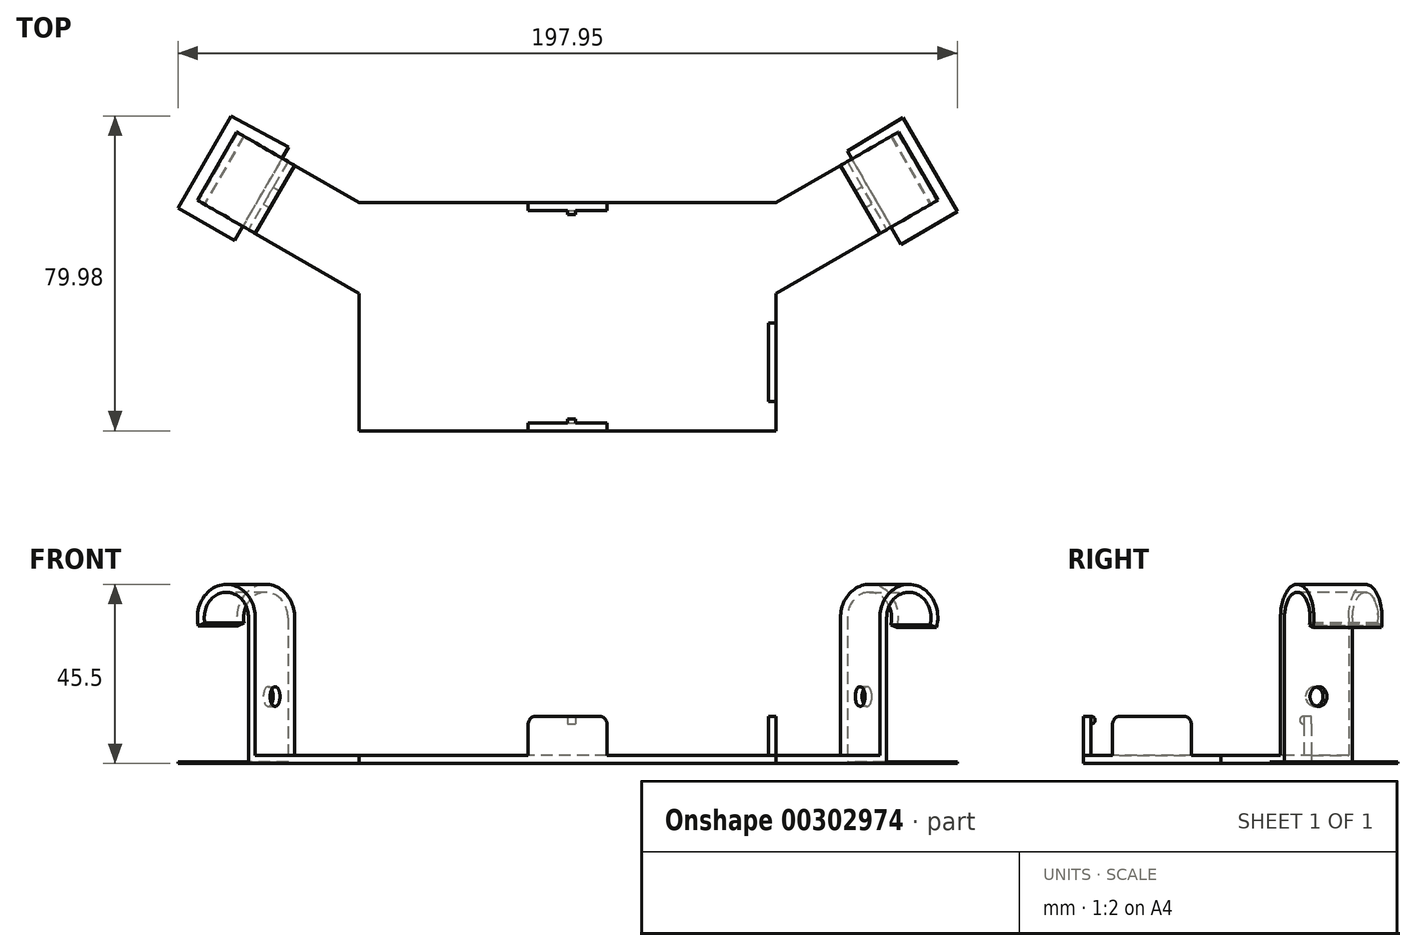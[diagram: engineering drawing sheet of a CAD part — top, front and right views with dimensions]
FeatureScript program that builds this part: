
annotation { "Feature Type Name" : "Feature", "Feature Type Description" : "" }
export const myFeature = defineFeature(function(context is Context, id is Id, definition is map)
    precondition{}
    {
        {
            var Q0;
            Q0=qCreatedBy(makeId("Top.planeOp"),FACE);
            var sketch = newSketch(context, id + "F0", { "sketchPlane" : qUnion([Q0])});
            skLineSegment(sketch, "E0.0", {"start": v(-14.9, 234.67) * mm, "end": v(190.1, -120.4) * mm, "construction": true});
            skLineSegment(sketch, "E0.1", {"start": v(190.1, -120.4) * mm, "end": v(-219.9, -120.4) * mm, "construction": true});
            skLineSegment(sketch, "E0.2", {"start": v(-219.9, -120.4) * mm, "end": v(-14.9, 234.67) * mm, "construction": true});
            skPoint(sketch, "E0.0.midPoint", {"position": v(87.6, 57.13) * mm});
            skPoint(sketch, "E1.endSnap0", {"position": v(-14.9, -120.4) * mm});
            skLineSegment(sketch, "E2", {"start": v(-14.9, 234.67) * mm, "end": v(-14.9, 59.17) * mm, "construction": true});
            skLineSegment(sketch, "E3.bottom", {"start": v(38.1, 30.17) * mm, "end": v(-67.9, 30.17) * mm});
            skLineSegment(sketch, "E3.top", {"start": v(38.1, 88.17) * mm, "end": v(-67.9, 88.17) * mm});
            skLineSegment(sketch, "E3.left", {"start": v(38.1, 30.17) * mm, "end": v(38.1, 88.17) * mm});
            skLineSegment(sketch, "E3.right", {"start": v(-67.9, 30.17) * mm, "end": v(-67.9, 88.17) * mm});
            skPoint(sketch, "E3.middle", {"position": v(-14.9, 59.17) * mm});
            skLineSegment(sketch, "E4", {"start": v(-67.9, 88.17) * mm, "end": v(-91.59, 101.84) * mm});
            skLineSegment(sketch, "E5", {"start": v(38.1, 88.17) * mm, "end": v(61.78, 101.84) * mm});
            skLineSegment(sketch, "E6", {"start": v(38.1, 65.07) * mm, "end": v(71.78, 84.52) * mm});
            skLineSegment(sketch, "E7", {"start": v(-67.9, 65.07) * mm, "end": v(-101.59, 84.52) * mm});
            skLineSegment(sketch, "E8", {"start": v(61.78, 101.84) * mm, "end": v(71.78, 84.52) * mm});
            skLineSegment(sketch, "E9", {"start": v(-91.59, 101.84) * mm, "end": v(-101.59, 84.52) * mm});
            skSolve(sketch);
        }
        {
            var Q0;
            {var subQ3=sQuery(id+"F0.wireOp",EDGE,"E3.bottom");Q0=makeQuery(id+"F0.imprint","IMPRINT",FACE,{"disambiguationData":[TD([[makeQuery(id+"F0.imprint","IMPRINT",EDGE,{"derivedFrom":subQ3}),-1.0]])]});}
            var Q1;
            {var subQ0=sQuery(id+"F0.wireOp",EDGE,"E4");Q1=makeQuery(id+"F0.imprint","IMPRINT",FACE,{"disambiguationData":[TD([[makeQuery(id+"F0.imprint","IMPRINT",EDGE,{"derivedFrom":subQ0}),1.0]])]});}
            var Q2;
            {var subQ0=sQuery(id+"F0.wireOp",EDGE,"E5");Q2=makeQuery(id+"F0.imprint","IMPRINT",FACE,{"disambiguationData":[TD([[makeQuery(id+"F0.imprint","IMPRINT",EDGE,{"derivedFrom":subQ0}),-1.0]])]});}
            extrude(context, id + "F1", {"entities" : qUnion([Q0, Q1, Q2]), "depth" : 2 * mm, "offsetDistance" : 25 * mm});
        }
        {
            var Q0;
            Q0=makeQuery(id+"F1.opExtrude","CAP_FACE",FACE,{"disambiguationData":[OSD([sQuery(id+"F0.wireOp",EDGE,"E3.bottom"),sQuery(id+"F0.wireOp",EDGE,"E3.top"),sQuery(id+"F0.wireOp",EDGE,"E3.left"),sQuery(id+"F0.wireOp",EDGE,"E3.right"),sQuery(id+"F0.wireOp",EDGE,"E4"),sQuery(id+"F0.wireOp",EDGE,"E5"),sQuery(id+"F0.wireOp",EDGE,"E6"),sQuery(id+"F0.wireOp",EDGE,"E7"),sQuery(id+"F0.wireOp",EDGE,"E8"),sQuery(id+"F0.wireOp",EDGE,"E9")])],"isStart":false});
            var sketch = newSketch(context, id + "F2", { "sketchPlane" : qUnion([Q0])});
            skLineSegment(sketch, "E10", {"start": v(-85.96, 98.6) * mm, "end": v(-95.96, 81.27) * mm});
            skLineSegment(sketch, "E11", {"start": v(-84.23, 97.6) * mm, "end": v(-94.23, 80.27) * mm});
            skLineSegment(sketch, "E12", {"start": v(-85.96, 98.6) * mm, "end": v(-84.23, 97.6) * mm});
            skLineSegment(sketch, "E13", {"start": v(-95.96, 81.27) * mm, "end": v(-94.23, 80.27) * mm});
            skLineSegment(sketch, "E14", {"start": v(56.15, 98.6) * mm, "end": v(66.15, 81.27) * mm});
            skLineSegment(sketch, "E15", {"start": v(54.42, 97.6) * mm, "end": v(64.42, 80.27) * mm});
            skLineSegment(sketch, "E16", {"start": v(54.42, 97.6) * mm, "end": v(56.15, 98.6) * mm});
            skLineSegment(sketch, "E17", {"start": v(66.15, 81.27) * mm, "end": v(64.42, 80.27) * mm});
            skSolve(sketch);
        }
        {
            var Q0;
            Q0=makeQuery(id+"F2.imprint","IMPRINT",FACE,{"disambiguationData":[TD([[makeQuery(id+"F2.imprint","IMPRINT",EDGE,{"derivedFrom":sQuery(id+"F2.wireOp",EDGE,"E10")}),1.0]])]});
            var Q1;
            Q1=makeQuery(id+"F2.imprint","IMPRINT",FACE,{"disambiguationData":[TD([[makeQuery(id+"F2.imprint","IMPRINT",EDGE,{"derivedFrom":sQuery(id+"F2.wireOp",EDGE,"E14")}),-1.0]])]});
            extrude(context, id + "F3", {"entities" : qUnion([Q0, Q1]), "operationType" : NewBodyOperationType.ADD, "depth" : 35 * mm, "offsetDistance" : 25 * mm});
        }
        {
            var Q0;
            Q0=makeQuery(id+"F3.boolean.opBoolean","MERGE",FACE,{"derivedFrom":[makeQuery(id+"F1.opExtrude","SWEPT_FACE",FACE,{"disambiguationData":[OSD([sQuery(id+"F0.wireOp",EDGE,"E6")])]}),makeQuery(id+"F3.opExtrude","SWEPT_FACE",FACE,{"disambiguationData":[OSD([sQuery(id+"F2.wireOp",EDGE,"E17")])]})]});
            var sketch = newSketch(context, id + "F4", { "sketchPlane" : qUnion([Q0])});
            skArc(sketch, "E18", {"start": v(110.68, 35.24) * mm, "mid": v(105.32, 43.44) * mm, "end": v(97.93, 37) * mm});
            skArc(sketch, "E19", {"start": v(112.57, 34.55) * mm, "mid": v(105.66, 45.4) * mm, "end": v(95.93, 37) * mm});
            skLineSegment(sketch, "E20", {"start": v(110.68, 35.24) * mm, "end": v(112.57, 34.55) * mm});
            skLineSegment(sketch, "E21", {"start": v(97.93, 37) * mm, "end": v(95.93, 37) * mm});
            skSolve(sketch);
        }
        {
            var Q0;
            Q0=makeQuery(id+"F4.imprint","IMPRINT",FACE,{"disambiguationData":[TD([[makeQuery(id+"F4.imprint","IMPRINT",EDGE,{"derivedFrom":sQuery(id+"F4.wireOp",EDGE,"E18")}),-1.0]])]});
            extrude(context, id + "F5", {"entities" : qUnion([Q0]), "operationType" : NewBodyOperationType.ADD, "oppositeDirection" : true, "depth" : 20 * mm, "offsetDistance" : 25 * mm});
        }
        {
            var Q0;
            Q0=makeQuery(id+"F5.boolean.opBoolean","MERGE",FACE,{"derivedFrom":[makeQuery(id+"F3.boolean.opBoolean","MERGE",FACE,{"derivedFrom":[makeQuery(id+"F1.opExtrude","SWEPT_FACE",FACE,{"disambiguationData":[OSD([sQuery(id+"F0.wireOp",EDGE,"E6")])]}),makeQuery(id+"F3.opExtrude","SWEPT_FACE",FACE,{"disambiguationData":[OSD([sQuery(id+"F2.wireOp",EDGE,"E17")])]})]}),makeQuery(id+"F5.opExtrude","CAP_FACE",FACE,{"disambiguationData":[OSD([sQuery(id+"F4.wireOp",EDGE,"E18"),sQuery(id+"F4.wireOp",EDGE,"E19"),sQuery(id+"F4.wireOp",EDGE,"E20"),sQuery(id+"F4.wireOp",EDGE,"E21")])],"isStart":true})]});
            var sketch = newSketch(context, id + "F6", { "sketchPlane" : qUnion([Q0])});
            skLineSegment(sketch, "E22.bottom", {"start": v(97.93, 2) * mm, "end": v(104.43, 2) * mm});
            skLineSegment(sketch, "E22.top", {"start": v(97.93, 0) * mm, "end": v(104.43, 0) * mm});
            skLineSegment(sketch, "E22.left", {"start": v(97.93, 2) * mm, "end": v(97.93, 0) * mm});
            skLineSegment(sketch, "E22.right", {"start": v(104.43, 2) * mm, "end": v(104.43, 0) * mm});
            skSolve(sketch);
        }
        {
            var Q0;
            Q0=makeQuery(id+"F6.imprint","IMPRINT",FACE,{"disambiguationData":[TD([[makeQuery(id+"F6.imprint","IMPRINT",EDGE,{"derivedFrom":sQuery(id+"F6.wireOp",EDGE,"E22.bottom")}),-1.0]])]});
            extrude(context, id + "F7", {"entities" : qUnion([Q0]), "operationType" : NewBodyOperationType.REMOVE, "oppositeDirection" : true, "depth" : 20 * mm, "offsetDistance" : 25 * mm});
        }
        {
            var Q0;
            Q0=makeQuery(id+"F3.boolean.opBoolean","MERGE",FACE,{"derivedFrom":[makeQuery(id+"F1.opExtrude","SWEPT_FACE",FACE,{"disambiguationData":[OSD([sQuery(id+"F0.wireOp",EDGE,"E7")])]}),makeQuery(id+"F3.opExtrude","SWEPT_FACE",FACE,{"disambiguationData":[OSD([sQuery(id+"F2.wireOp",EDGE,"E13")])]})]});
            var sketch = newSketch(context, id + "F8", { "sketchPlane" : qUnion([Q0])});
            skLineSegment(sketch, "E23", {"start": v(-121.74, 37) * mm, "end": v(-123.74, 37) * mm});
            skArc(sketch, "E24", {"start": v(-123.74, 37) * mm, "mid": v(-130.9, 43.47) * mm, "end": v(-136.6, 35.68) * mm});
            skArc(sketch, "E25", {"start": v(-121.74, 37) * mm, "mid": v(-131.25, 45.44) * mm, "end": v(-138.5, 34.99) * mm});
            skLineSegment(sketch, "E26", {"start": v(-136.6, 35.68) * mm, "end": v(-138.5, 34.99) * mm});
            skSolve(sketch);
        }
        {
            var Q0;
            Q0=makeQuery(id+"F8.imprint","IMPRINT",FACE,{"disambiguationData":[TD([[makeQuery(id+"F8.imprint","IMPRINT",EDGE,{"derivedFrom":sQuery(id+"F8.wireOp",EDGE,"E23")}),-1.0]])]});
            extrude(context, id + "F9", {"entities" : qUnion([Q0]), "operationType" : NewBodyOperationType.ADD, "oppositeDirection" : true, "depth" : 20 * mm, "offsetDistance" : 25 * mm});
        }
        {
            var Q0;
            Q0=makeQuery(id+"F9.boolean.opBoolean","MERGE",FACE,{"derivedFrom":[makeQuery(id+"F3.boolean.opBoolean","MERGE",FACE,{"derivedFrom":[makeQuery(id+"F1.opExtrude","SWEPT_FACE",FACE,{"disambiguationData":[OSD([sQuery(id+"F0.wireOp",EDGE,"E7")])]}),makeQuery(id+"F3.opExtrude","SWEPT_FACE",FACE,{"disambiguationData":[OSD([sQuery(id+"F2.wireOp",EDGE,"E13")])]})]}),makeQuery(id+"F9.opExtrude","CAP_FACE",FACE,{"disambiguationData":[OSD([sQuery(id+"F8.wireOp",EDGE,"E23"),sQuery(id+"F8.wireOp",EDGE,"E24"),sQuery(id+"F8.wireOp",EDGE,"E25"),sQuery(id+"F8.wireOp",EDGE,"E26")])],"isStart":true})]});
            var sketch = newSketch(context, id + "F10", { "sketchPlane" : qUnion([Q0])});
            skLineSegment(sketch, "E27.bottom", {"start": v(-123.74, 2) * mm, "end": v(-130.24, 2) * mm});
            skLineSegment(sketch, "E27.top", {"start": v(-123.74, 0) * mm, "end": v(-130.24, 0) * mm});
            skLineSegment(sketch, "E27.left", {"start": v(-123.74, 2) * mm, "end": v(-123.74, 0) * mm});
            skLineSegment(sketch, "E27.right", {"start": v(-130.24, 2) * mm, "end": v(-130.24, 0) * mm});
            skSolve(sketch);
        }
        {
            var Q0;
            Q0=makeQuery(id+"F10.imprint","IMPRINT",FACE,{"disambiguationData":[TD([[makeQuery(id+"F10.imprint","IMPRINT",EDGE,{"derivedFrom":sQuery(id+"F10.wireOp",EDGE,"E27.bottom")}),1.0]])]});
            extrude(context, id + "F11", {"entities" : qUnion([Q0]), "operationType" : NewBodyOperationType.REMOVE, "oppositeDirection" : true, "depth" : 20 * mm, "offsetDistance" : 25 * mm});
        }
        {
            var Q0;
            Q0=makeQuery(id+"F3.opExtrude","SWEPT_FACE",FACE,{"disambiguationData":[OSD([sQuery(id+"F2.wireOp",EDGE,"E11")])]});
            var sketch = newSketch(context, id + "F12", { "sketchPlane" : qUnion([Q0])});
            skLineSegment(sketch, "E28", {"start": v(32.4, 37) * mm, "end": v(32.4, 17) * mm, "construction": true});
            skCircle(sketch, "E29", {"center": v(32.4, 17) * mm, "radius": 2.5 * mm});
            skSolve(sketch);
        }
        {
            var Q0;
            Q0=makeQuery(id+"F12.imprint","IMPRINT",FACE,{"disambiguationData":[TD([[makeQuery(id+"F12.imprint","IMPRINT",EDGE,{"derivedFrom":sQuery(id+"F12.wireOp",EDGE,"E29")}),1.0]])]});
            extrude(context, id + "F13", {"entities" : qUnion([Q0]), "operationType" : NewBodyOperationType.REMOVE, "oppositeDirection" : true, "depth" : 2 * mm, "offsetDistance" : 25 * mm});
        }
        {
            var Q0;
            Q0=makeQuery(id+"F3.opExtrude","SWEPT_FACE",FACE,{"disambiguationData":[OSD([sQuery(id+"F2.wireOp",EDGE,"E15")])]});
            var sketch = newSketch(context, id + "F14", { "sketchPlane" : qUnion([Q0])});
            skLineSegment(sketch, "E30", {"start": v(-47.3, 37) * mm, "end": v(-47.3, 17) * mm, "construction": true});
            skPoint(sketch, "E30.endSnap0", {"position": v(-47.3, 37) * mm});
            skCircle(sketch, "E31", {"center": v(-47.3, 17) * mm, "radius": 2.5 * mm});
            skSolve(sketch);
        }
        {
            var Q0;
            Q0=makeQuery(id+"F14.imprint","IMPRINT",FACE,{"disambiguationData":[TD([[makeQuery(id+"F14.imprint","IMPRINT",EDGE,{"derivedFrom":sQuery(id+"F14.wireOp",EDGE,"E31")}),1.0]])]});
            extrude(context, id + "F15", {"entities" : qUnion([Q0]), "operationType" : NewBodyOperationType.REMOVE, "oppositeDirection" : true, "depth" : 2 * mm, "offsetDistance" : 25 * mm});
        }
        {
            var Q0;
            {var subQ0=sQuery(id+"F0.wireOp",EDGE,"E7");var subQ1=sQuery(id+"F0.wireOp",EDGE,"E6");var subQ2=sQuery(id+"F0.wireOp",EDGE,"E5");var subQ3=sQuery(id+"F0.wireOp",EDGE,"E4");var subQ4=sQuery(id+"F0.wireOp",EDGE,"E3.bottom");var subQ5=sQuery(id+"F0.wireOp",EDGE,"E3.right");var subQ6=sQuery(id+"F0.wireOp",EDGE,"E3.top");var subQ7=sQuery(id+"F0.wireOp",EDGE,"E3.left");Q0=makeQuery(id+"F3.boolean.opBoolean","SPLIT",FACE,{"disambiguationData":[TD([makeQuery(id+"F1.opExtrude","SWEPT_FACE",FACE,{"disambiguationData":[OSD([subQ4])]})])],"derivedFrom":makeQuery(id+"F1.opExtrude","CAP_FACE",FACE,{"disambiguationData":[OSD([subQ4,subQ6,subQ7,subQ5,subQ3,subQ2,subQ1,subQ0,sQuery(id+"F0.wireOp",EDGE,"E8"),sQuery(id+"F0.wireOp",EDGE,"E9")])],"isStart":false})});}
            var sketch = newSketch(context, id + "F16", { "sketchPlane" : qUnion([Q0])});
            skLineSegment(sketch, "E32.bottom", {"start": v(-4.9, 32.17) * mm, "end": v(-24.9, 32.17) * mm});
            skLineSegment(sketch, "E32.left", {"start": v(-4.9, 32.17) * mm, "end": v(-4.9, 30.17) * mm});
            skLineSegment(sketch, "E32.right", {"start": v(-24.9, 32.17) * mm, "end": v(-24.9, 30.17) * mm});
            skPoint(sketch, "E32.middle", {"position": v(-14.9, 30.17) * mm});
            skLineSegment(sketch, "E33.top", {"start": v(-4.9, 86.17) * mm, "end": v(-24.9, 86.17) * mm});
            skLineSegment(sketch, "E33.left", {"start": v(-4.9, 88.17) * mm, "end": v(-4.9, 86.17) * mm});
            skLineSegment(sketch, "E33.right", {"start": v(-24.9, 88.17) * mm, "end": v(-24.9, 86.17) * mm});
            skPoint(sketch, "E33.middle", {"position": v(-14.9, 88.17) * mm});
            skLineSegment(sketch, "E34", {"start": v(-4.9, 88.17) * mm, "end": v(-24.9, 88.17) * mm});
            skLineSegment(sketch, "E35", {"start": v(-4.9, 30.17) * mm, "end": v(-24.9, 30.17) * mm});
            skPoint(sketch, "E33.bottom.start.orphan", {"position": v(-4.9, 90.17) * mm});
            skPoint(sketch, "E36.orphan", {"position": v(-24.9, 90.17) * mm});
            skPoint(sketch, "E32.top.start.orphan", {"position": v(-4.9, 28.17) * mm});
            skPoint(sketch, "E37.orphan", {"position": v(-24.9, 28.17) * mm});
            skLineSegment(sketch, "E38.bottom", {"start": v(36.1, 57.62) * mm, "end": v(38.1, 57.62) * mm});
            skLineSegment(sketch, "E38.top", {"start": v(36.1, 37.62) * mm, "end": v(38.1, 37.62) * mm});
            skLineSegment(sketch, "E38.left", {"start": v(36.1, 57.62) * mm, "end": v(36.1, 37.62) * mm});
            skPoint(sketch, "E38.middle", {"position": v(38.1, 47.62) * mm});
            skLineSegment(sketch, "E39", {"start": v(38.1, 37.62) * mm, "end": v(38.1, 57.62) * mm});
            skPoint(sketch, "E38.right.end.orphan", {"position": v(40.1, 37.62) * mm});
            skPoint(sketch, "E40.orphan", {"position": v(40.1, 57.62) * mm});
            skSolve(sketch);
        }
        {
            var Q0;
            Q0=makeQuery(id+"F16.imprint","IMPRINT",FACE,{"disambiguationData":[TD([[makeQuery(id+"F16.imprint","IMPRINT",EDGE,{"derivedFrom":sQuery(id+"F16.wireOp",EDGE,"E33.top")}),-1.0]])]});
            var Q1;
            Q1=makeQuery(id+"F16.imprint","IMPRINT",FACE,{"disambiguationData":[TD([[makeQuery(id+"F16.imprint","IMPRINT",EDGE,{"derivedFrom":sQuery(id+"F16.wireOp",EDGE,"E32.bottom")}),1.0]])]});
            var Q2;
            Q2=makeQuery(id+"F16.imprint","IMPRINT",FACE,{"disambiguationData":[TD([[makeQuery(id+"F16.imprint","IMPRINT",EDGE,{"derivedFrom":sQuery(id+"F16.wireOp",EDGE,"E38.bottom")}),-1.0]])]});
            extrude(context, id + "F17", {"entities" : qUnion([Q0, Q1, Q2]), "operationType" : NewBodyOperationType.ADD, "depth" : 10 * mm, "offsetDistance" : 25 * mm});
        }
        {
            var Q0;
            Q0=makeQuery(id+"F17.opExtrude","CAP_EDGE",EDGE,{"disambiguationData":[OSD([sQuery(id+"F16.wireOp",EDGE,"E33.right")])],"isStart":false});
            var Q1;
            Q1=makeQuery(id+"F17.opExtrude","CAP_EDGE",EDGE,{"disambiguationData":[OSD([sQuery(id+"F16.wireOp",EDGE,"E33.left")])],"isStart":false});
            var Q2;
            Q2=makeQuery(id+"F17.opExtrude","CAP_EDGE",EDGE,{"disambiguationData":[OSD([sQuery(id+"F16.wireOp",EDGE,"E32.right")])],"isStart":false});
            var Q3;
            Q3=makeQuery(id+"F17.opExtrude","CAP_EDGE",EDGE,{"disambiguationData":[OSD([sQuery(id+"F16.wireOp",EDGE,"E32.left")])],"isStart":false});
            var Q4;
            Q4=makeQuery(id+"F17.opExtrude","CAP_EDGE",EDGE,{"disambiguationData":[OSD([sQuery(id+"F16.wireOp",EDGE,"E38.top")])],"isStart":false});
            var Q5;
            Q5=makeQuery(id+"F17.opExtrude","CAP_EDGE",EDGE,{"disambiguationData":[OSD([sQuery(id+"F16.wireOp",EDGE,"E38.bottom")])],"isStart":false});
            fillet(context, id + "F18", {"entities" : qUnion([Q0, Q1, Q2, Q3, Q4, Q5]), "radius" : 2 * mm, "tangentPropagation" : true, "allowEdgeOverflow" : false});
        }
        {
            var Q0;
            Q0=makeQuery(id+"F17.opExtrude","SWEPT_FACE",FACE,{"disambiguationData":[OSD([sQuery(id+"F16.wireOp",EDGE,"E33.top")])]});
            var sketch = newSketch(context, id + "F19", { "sketchPlane" : qUnion([Q0])});
            skLineSegment(sketch, "E41.bottom", {"start": v(-14.9, 12) * mm, "end": v(-12.9, 12) * mm});
            skLineSegment(sketch, "E41.top", {"start": v(-14.9, 10) * mm, "end": v(-12.9, 10) * mm});
            skLineSegment(sketch, "E41.left", {"start": v(-14.9, 12) * mm, "end": v(-14.9, 10) * mm});
            skLineSegment(sketch, "E41.right", {"start": v(-12.9, 12) * mm, "end": v(-12.9, 10) * mm});
            skSolve(sketch);
        }
        {
            var Q0;
            Q0=makeQuery(id+"F19.imprint","IMPRINT",FACE,{"disambiguationData":[TD([[makeQuery(id+"F19.imprint","IMPRINT",EDGE,{"derivedFrom":sQuery(id+"F19.wireOp",EDGE,"E41.bottom")}),1.0]])]});
            extrude(context, id + "F20", {"entities" : qUnion([Q0]), "operationType" : NewBodyOperationType.ADD, "depth" : 1 * mm, "offsetDistance" : 25 * mm});
        }
        {
            var Q0;
            Q0=makeQuery(id+"F20.opExtrude","CAP_EDGE",EDGE,{"disambiguationData":[OSD([sQuery(id+"F19.wireOp",EDGE,"E41.top")])],"isStart":false});
            var Q1;
            Q1=makeQuery(id+"F20.opExtrude","CAP_EDGE",EDGE,{"disambiguationData":[OSD([sQuery(id+"F19.wireOp",EDGE,"E41.bottom")])],"isStart":false});
            fillet(context, id + "F21", {"entities" : qUnion([Q0, Q1]), "radius" : 1 * mm, "tangentPropagation" : true, "allowEdgeOverflow" : false});
        }
        {
            var Q0;
            Q0=makeQuery(id+"F17.opExtrude","SWEPT_FACE",FACE,{"disambiguationData":[OSD([sQuery(id+"F16.wireOp",EDGE,"E32.bottom")])]});
            var sketch = newSketch(context, id + "F22", { "sketchPlane" : qUnion([Q0])});
            skLineSegment(sketch, "E42.bottom", {"start": v(14.9, 12) * mm, "end": v(12.9, 12) * mm});
            skLineSegment(sketch, "E42.top", {"start": v(14.9, 10) * mm, "end": v(12.9, 10) * mm});
            skLineSegment(sketch, "E42.left", {"start": v(14.9, 12) * mm, "end": v(14.9, 10) * mm});
            skLineSegment(sketch, "E42.right", {"start": v(12.9, 12) * mm, "end": v(12.9, 10) * mm});
            skSolve(sketch);
        }
        {
            var Q0;
            Q0=makeQuery(id+"F22.imprint","IMPRINT",FACE,{"disambiguationData":[TD([[makeQuery(id+"F22.imprint","IMPRINT",EDGE,{"derivedFrom":sQuery(id+"F22.wireOp",EDGE,"E42.bottom")}),-1.0]])]});
            extrude(context, id + "F23", {"entities" : qUnion([Q0]), "operationType" : NewBodyOperationType.ADD, "depth" : 1 * mm, "offsetDistance" : 25 * mm});
        }
        {
            var Q0;
            Q0=makeQuery(id+"F23.opExtrude","CAP_EDGE",EDGE,{"disambiguationData":[OSD([sQuery(id+"F22.wireOp",EDGE,"E42.top")])],"isStart":false});
            var Q1;
            Q1=makeQuery(id+"F23.opExtrude","CAP_EDGE",EDGE,{"disambiguationData":[OSD([sQuery(id+"F22.wireOp",EDGE,"E42.bottom")])],"isStart":false});
            fillet(context, id + "F24", {"entities" : qUnion([Q0, Q1]), "radius" : 1 * mm, "tangentPropagation" : true, "allowEdgeOverflow" : false});
        }
        {
            var Q0;
            Q0=makeQuery(id+"F1.opExtrude","CAP_FACE",FACE,{"disambiguationData":[OSD([sQuery(id+"F0.wireOp",EDGE,"E3.bottom"),sQuery(id+"F0.wireOp",EDGE,"E3.top"),sQuery(id+"F0.wireOp",EDGE,"E3.left"),sQuery(id+"F0.wireOp",EDGE,"E3.right"),sQuery(id+"F0.wireOp",EDGE,"E4"),sQuery(id+"F0.wireOp",EDGE,"E5"),sQuery(id+"F0.wireOp",EDGE,"E6"),sQuery(id+"F0.wireOp",EDGE,"E7"),sQuery(id+"F0.wireOp",EDGE,"E8"),sQuery(id+"F0.wireOp",EDGE,"E9")])],"isStart":true});
            var sketch = newSketch(context, id + "F25", { "sketchPlane" : qUnion([Q0])});
            skLineSegment(sketch, "E43", {"start": v(-85.83, -102.23) * mm, "end": v(-99.5, -78.56) * mm});
            skLineSegment(sketch, "E44", {"start": v(-99.5, -78.56) * mm, "end": v(-113.85, -86.84) * mm});
            skLineSegment(sketch, "E45", {"start": v(-113.85, -86.84) * mm, "end": v(-100.39, -110.15) * mm});
            skLineSegment(sketch, "E46", {"start": v(-100.39, -110.15) * mm, "end": v(-85.83, -102.23) * mm});
            skLineSegment(sketch, "E47", {"start": v(56.15, -101.2) * mm, "end": v(69.8, -77.57) * mm});
            skLineSegment(sketch, "E48", {"start": v(69.8, -77.57) * mm, "end": v(84.1, -85.83) * mm});
            skLineSegment(sketch, "E49", {"start": v(84.1, -85.83) * mm, "end": v(70.3, -109.73) * mm});
            skLineSegment(sketch, "E50", {"start": v(70.3, -109.73) * mm, "end": v(56.15, -101.2) * mm});
            skSolve(sketch);
        }
        {
            var Q0;
            Q0=makeQuery(id+"F25.imprint","IMPRINT",FACE,{"disambiguationData":[TD([[makeQuery(id+"F25.imprint","IMPRINT",EDGE,{"derivedFrom":sQuery(id+"F25.wireOp",EDGE,"E47")}),-1.0]])]});
            var Q1;
            Q1=makeQuery(id+"F25.imprint","IMPRINT",FACE,{"disambiguationData":[TD([[makeQuery(id+"F25.imprint","IMPRINT",EDGE,{"derivedFrom":sQuery(id+"F25.wireOp",EDGE,"E43")}),1.0]])]});
            extrude(context, id + "F26", {"entities" : qUnion([Q0, Q1]), "oppositeDirection" : true, "depth" : 0.4 * mm, "offsetDistance" : 25 * mm});
        }
    });
